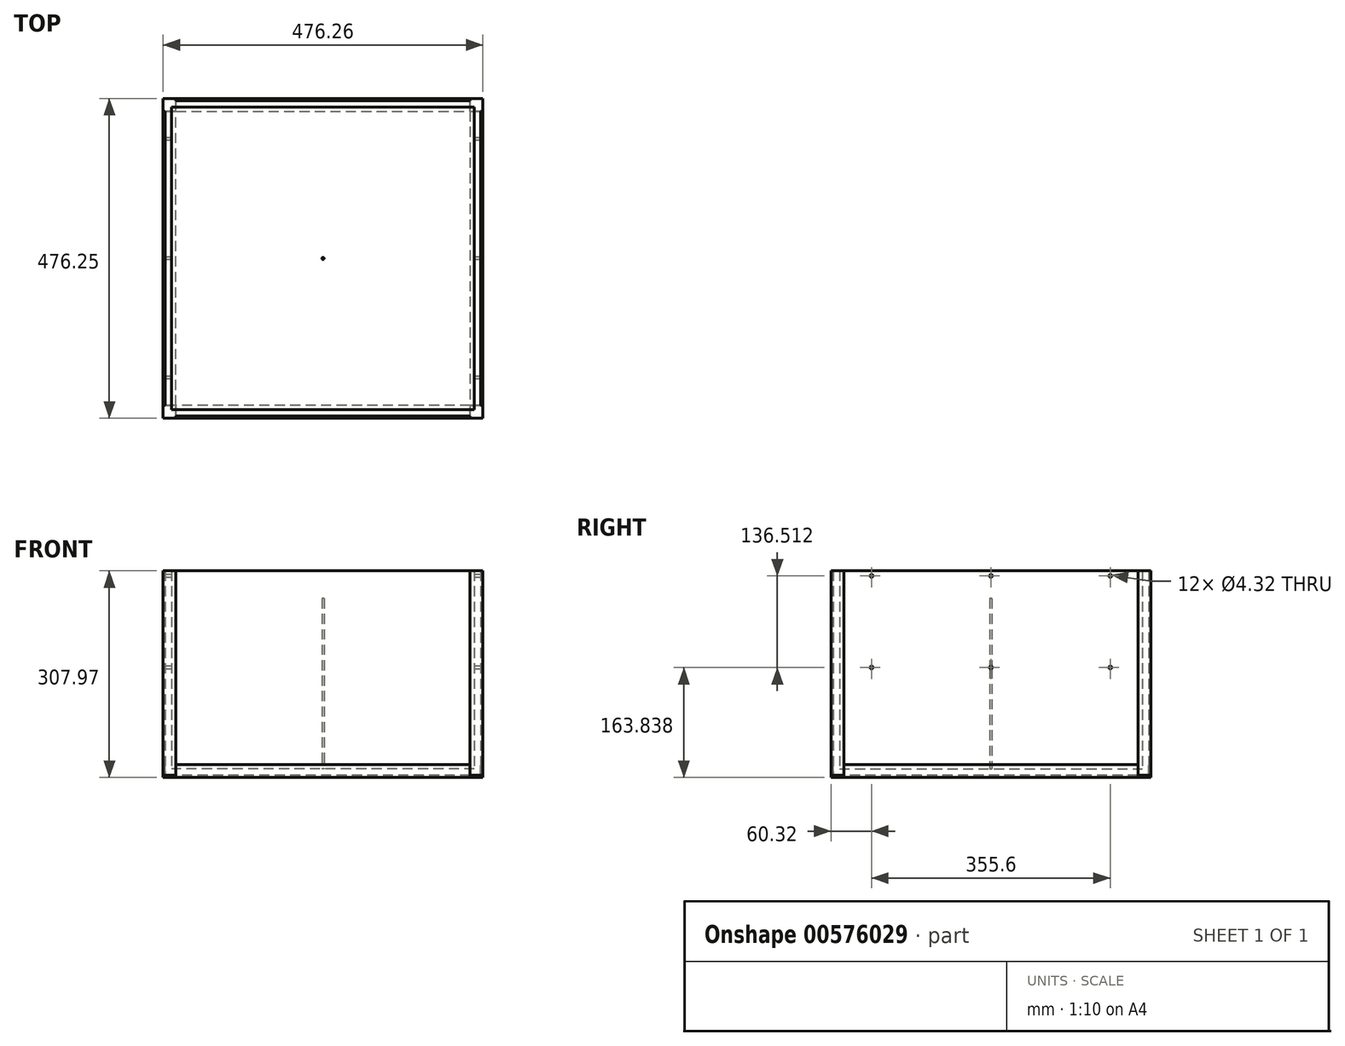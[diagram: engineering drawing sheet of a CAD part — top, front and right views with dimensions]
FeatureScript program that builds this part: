
annotation { "Feature Type Name" : "Feature", "Feature Type Description" : "" }
export const myFeature = defineFeature(function(context is Context, id is Id, definition is map)
    precondition{}
    {
        {
            var Q0;
            Q0=qCreatedBy(makeId("Top.planeOp"),FACE);
            var sketch = newSketch(context, id + "F0", { "sketchPlane" : qUnion([Q0])});
            skLineSegment(sketch, "E0.bottom", {"start": v(234.95, -234.95) * mm, "end": v(-234.95, -234.95) * mm});
            skLineSegment(sketch, "E0.top", {"start": v(234.95, 234.95) * mm, "end": v(-234.95, 234.95) * mm});
            skLineSegment(sketch, "E0.left", {"start": v(234.95, -234.95) * mm, "end": v(234.95, 234.95) * mm});
            skLineSegment(sketch, "E0.right", {"start": v(-234.95, -234.95) * mm, "end": v(-234.95, 234.95) * mm});
            skPoint(sketch, "E0.middle", {"position": v(0, 0) * mm});
            skLineSegment(sketch, "E1", {"start": v(-234.95, 238.13) * mm, "end": v(-238.13, 238.13) * mm});
            skLineSegment(sketch, "E2", {"start": v(-238.13, 238.13) * mm, "end": v(-238.13, 219.08) * mm});
            skLineSegment(sketch, "E3", {"start": v(-238.13, 219.08) * mm, "end": v(-234.95, 219.08) * mm});
            skLineSegment(sketch, "E4", {"start": v(-238.13, 238.13) * mm, "end": v(-219.08, 238.13) * mm});
            skLineSegment(sketch, "E5", {"start": v(-219.08, 238.13) * mm, "end": v(-219.08, 234.95) * mm});
            skLineSegment(sketch, "E6.1.0", {"start": v(-238.13, -238.13) * mm, "end": v(-238.13, -219.08) * mm});
            skLineSegment(sketch, "E6.1.1", {"start": v(-238.13, -238.13) * mm, "end": v(-219.08, -238.13) * mm});
            skLineSegment(sketch, "E6.1.2", {"start": v(-219.08, -238.13) * mm, "end": v(-219.08, -234.95) * mm});
            skLineSegment(sketch, "E6.1.3", {"start": v(-238.13, -219.08) * mm, "end": v(-234.95, -219.08) * mm});
            skLineSegment(sketch, "E6.1.4", {"start": v(-238.13, -234.95) * mm, "end": v(-238.13, -238.13) * mm});
            skLineSegment(sketch, "E6.2.0", {"start": v(238.13, -238.13) * mm, "end": v(219.08, -238.13) * mm});
            skLineSegment(sketch, "E6.2.1", {"start": v(238.13, -238.13) * mm, "end": v(238.13, -219.08) * mm});
            skLineSegment(sketch, "E6.2.2", {"start": v(238.13, -219.08) * mm, "end": v(234.95, -219.08) * mm});
            skLineSegment(sketch, "E6.2.3", {"start": v(219.08, -238.13) * mm, "end": v(219.08, -234.95) * mm});
            skLineSegment(sketch, "E6.2.4", {"start": v(234.95, -238.13) * mm, "end": v(238.13, -238.13) * mm});
            skLineSegment(sketch, "E6.3.0", {"start": v(238.13, 238.13) * mm, "end": v(238.13, 219.08) * mm});
            skLineSegment(sketch, "E6.3.1", {"start": v(238.13, 238.13) * mm, "end": v(219.08, 238.13) * mm});
            skLineSegment(sketch, "E6.3.2", {"start": v(219.08, 238.13) * mm, "end": v(219.08, 234.95) * mm});
            skLineSegment(sketch, "E6.3.3", {"start": v(238.13, 219.08) * mm, "end": v(234.95, 219.08) * mm});
            skLineSegment(sketch, "E6.3.4", {"start": v(238.13, 234.95) * mm, "end": v(238.13, 238.13) * mm});
            skLineSegment(sketch, "E7.0", {"start": v(225.43, 225.43) * mm, "end": v(-225.42, 225.42) * mm});
            skLineSegment(sketch, "E7.1", {"start": v(225.43, -225.42) * mm, "end": v(225.43, 225.42) * mm});
            skLineSegment(sketch, "E7.2", {"start": v(225.43, -225.42) * mm, "end": v(-225.43, -225.43) * mm});
            skLineSegment(sketch, "E7.3", {"start": v(-225.43, -225.43) * mm, "end": v(-225.42, 225.42) * mm});
            skSolve(sketch);
        }
        {
            var Q0;
            Q0=qSketchRegion(id+"F0",true);
            extrude(context, id + "F1", {"entities" : qUnion([Q0]), "depth" : 304.8 * mm, "offsetDistance" : 25.4 * mm});
        }
        {
            var Q0;
            Q0=makeQuery(id+"F0.imprint","IMPRINT",FACE,{"disambiguationData":[TD([[makeQuery(id+"F0.imprint","IMPRINT",EDGE,{"derivedFrom":sQuery(id+"F0.wireOp",EDGE,"E7.0")}),1.0]])]});
            extrude(context, id + "F2", {"entities" : qUnion([Q0]), "operationType" : NewBodyOperationType.ADD, "depth" : 9.52 * mm, "offsetDistance" : 25.4 * mm});
        }
        {
            var Q0;
            Q0=makeQuery(id+"F1.opExtrude","SWEPT_FACE",FACE,{"disambiguationData":[OSD([sQuery(id+"F0.wireOp",EDGE,"E0.right")])]});
            var sketch = newSketch(context, id + "F3", { "sketchPlane" : qUnion([Q0])});
            skLineSegment(sketch, "E8", {"start": v(0, 304.8) * mm, "end": v(0, 297.18) * mm});
            skLineSegment(sketch, "E9", {"start": v(0, 304.8) * mm, "end": v(-177.8, 304.8) * mm});
            skLineSegment(sketch, "E10", {"start": v(-177.8, 304.8) * mm, "end": v(-177.8, 297.18) * mm});
            skLineSegment(sketch, "E11", {"start": v(0, 297.18) * mm, "end": v(0, 160.67) * mm});
            skLineSegment(sketch, "E12", {"start": v(-177.8, 297.18) * mm, "end": v(-177.8, 160.67) * mm});
            skLineSegment(sketch, "E13.MirrorCS", {"start": v(177.8, 304.8) * mm, "end": v(177.8, 297.18) * mm});
            skLineSegment(sketch, "E14.MirrorCS", {"start": v(177.8, 297.18) * mm, "end": v(177.8, 160.67) * mm});
            skLineSegment(sketch, "E15.MirrorCS", {"start": v(0, 304.8) * mm, "end": v(177.8, 304.8) * mm});
            skSolve(sketch);
        }
        {
            var Q0;
            Q0=sQuery(id+"F3.wireOp",VERTEX,"E12.start");
            var Q1;
            Q1=sQuery(id+"F3.wireOp",VERTEX,"E12.end");
            var Q2;
            Q2=sQuery(id+"F3.wireOp",VERTEX,"E8.end");
            var Q3;
            Q3=sQuery(id+"F3.wireOp",VERTEX,"E11.end");
            var Q4;
            Q4=sQuery(id+"F3.wireOp",VERTEX,"E14.MirrorCS.start");
            var Q5;
            Q5=sQuery(id+"F3.wireOp",VERTEX,"E14.MirrorCS.end");
            var Q6;
            Q6=makeQuery(id+"F1.opExtrude","SWEPT_BODY",BODY,{"disambiguationData":[OSD([sQuery(id+"F0.wireOp",EDGE,"E0.bottom"),sQuery(id+"F0.wireOp",EDGE,"E0.top"),sQuery(id+"F0.wireOp",EDGE,"E0.left"),sQuery(id+"F0.wireOp",EDGE,"E0.right"),sQuery(id+"F0.wireOp",EDGE,"E2"),sQuery(id+"F0.wireOp",EDGE,"E3"),sQuery(id+"F0.wireOp",EDGE,"E4"),sQuery(id+"F0.wireOp",EDGE,"E5"),sQuery(id+"F0.wireOp",EDGE,"E6.1.0"),sQuery(id+"F0.wireOp",EDGE,"E6.1.1"),sQuery(id+"F0.wireOp",EDGE,"E6.1.2"),sQuery(id+"F0.wireOp",EDGE,"E6.1.3"),sQuery(id+"F0.wireOp",EDGE,"E6.1.4"),sQuery(id+"F0.wireOp",EDGE,"E6.2.0"),sQuery(id+"F0.wireOp",EDGE,"E6.2.1"),sQuery(id+"F0.wireOp",EDGE,"E6.2.2"),sQuery(id+"F0.wireOp",EDGE,"E6.2.3"),sQuery(id+"F0.wireOp",EDGE,"E6.2.4"),sQuery(id+"F0.wireOp",EDGE,"E6.3.0"),sQuery(id+"F0.wireOp",EDGE,"E6.3.1"),sQuery(id+"F0.wireOp",EDGE,"E6.3.2"),sQuery(id+"F0.wireOp",EDGE,"E6.3.3"),sQuery(id+"F0.wireOp",EDGE,"E6.3.4"),sQuery(id+"F0.wireOp",EDGE,"E7.0"),sQuery(id+"F0.wireOp",EDGE,"E7.1"),sQuery(id+"F0.wireOp",EDGE,"E7.2"),sQuery(id+"F0.wireOp",EDGE,"E7.3")])]});
            hole(context, id + "F4", {"style" : HoleStyle.SIMPLE, "endStyle" : HoleEndStyle.BLIND, "standardTappedOrClearance" : lookupTablePath({ "standard" : "ANSI", "fit" : "Close", "size" : "#8", "type" : "Clearance" }), "standardBlindInLast" : lookupTablePath({ "fit" : "Close", "standard" : "ANSI", "size" : "#8", "type" : "Clearance" }), "holeDiameter" : 4.32 * mm, "holeDepth" : 762 * mm, "isTappedThrough" : true, "tappedDepth" : 12.7 * mm, "tapClearance" : 3, "locations" : qUnion([Q0, Q1, Q2, Q3, Q4, Q5]), "scope" : qUnion([Q6])});
        }
        {
            var Q0;
            Q0=makeQuery(id+"F1.opExtrude","SWEPT_FACE",FACE,{"disambiguationData":[OSD([sQuery(id+"F0.wireOp",EDGE,"E6.1.2")])]});
            var sketch = newSketch(context, id + "F5", { "sketchPlane" : qUnion([Q0])});
            skLineSegment(sketch, "E16", {"start": v(-238.12, -3.17) * mm, "end": v(-238.12, 15.87) * mm});
            skLineSegment(sketch, "E17", {"start": v(-238.12, 15.87) * mm, "end": v(-234.95, 15.87) * mm});
            skLineSegment(sketch, "E18", {"start": v(-234.95, 15.87) * mm, "end": v(-234.95, 0) * mm});
            skLineSegment(sketch, "E19", {"start": v(-234.95, 0) * mm, "end": v(-219.07, 0) * mm});
            skLineSegment(sketch, "E20", {"start": v(-219.07, 0) * mm, "end": v(-219.07, -3.17) * mm});
            skLineSegment(sketch, "E21", {"start": v(-219.07, -3.17) * mm, "end": v(-238.12, -3.17) * mm});
            skSolve(sketch);
        }
        {
            var Q0;
            Q0=qSketchRegion(id+"F5",true);
            var Q1;
            Q1=makeQuery(id+"F1.opExtrude","SWEPT_FACE",FACE,{"disambiguationData":[OSD([sQuery(id+"F0.wireOp",EDGE,"E6.2.3")])]});
            extrude(context, id + "F6", {"entities" : qUnion([Q0]), "endBound" : BoundingType.UP_TO_SURFACE, "depth" : 25.4 * mm, "endBoundEntityFace" : qUnion([Q1]), "offsetDistance" : 25.4 * mm});
        }
        {
            var Q0;
            Q0=makeQuery(id+"F2.opExtrude","CAP_FACE",FACE,{"disambiguationData":[OSD([sQuery(id+"F0.wireOp",EDGE,"E7.0"),sQuery(id+"F0.wireOp",EDGE,"E7.1"),sQuery(id+"F0.wireOp",EDGE,"E7.2"),sQuery(id+"F0.wireOp",EDGE,"E7.3")])],"isStart":false});
            var sketch = newSketch(context, id + "F7", { "sketchPlane" : qUnion([Q0])});
            skCircle(sketch, "E22", {"center": v(0, 0) * mm, "radius": 1.59 * mm});
            skSolve(sketch);
        }
        {
            var Q0;
            Q0=qSketchRegion(id+"F7",true);
            extrude(context, id + "F8", {"entities" : qUnion([Q0]), "operationType" : NewBodyOperationType.ADD, "depth" : 254 * mm, "offsetDistance" : 25.4 * mm});
        }
        {
            var Q0;
            Q0=makeQuery(id+"F6.opExtrude","SWEPT_BODY",BODY,{"disambiguationData":[OSD([sQuery(id+"F5.wireOp",EDGE,"E16"),sQuery(id+"F5.wireOp",EDGE,"E17"),sQuery(id+"F5.wireOp",EDGE,"E18"),sQuery(id+"F5.wireOp",EDGE,"E19"),sQuery(id+"F5.wireOp",EDGE,"E20"),sQuery(id+"F5.wireOp",EDGE,"E21")])]});
            var Q1;
            Q1=makeQuery(id+"F8.opExtrude","SWEPT_FACE",FACE,{"disambiguationData":[OSD([sQuery(id+"F7.wireOp",EDGE,"E22")])]});
            circularPattern(context, id + "F9", {"entities" : qUnion([Q0]), "axis" : qUnion([Q1]), "angle" : 360 * degree, "instanceCount" : 4, "equalSpace" : true});
        }
    });
